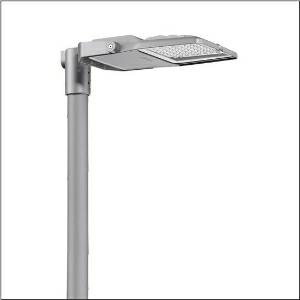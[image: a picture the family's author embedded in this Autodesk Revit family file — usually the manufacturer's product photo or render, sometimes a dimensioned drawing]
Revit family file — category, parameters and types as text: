
# Revit family: floodlight_fl_21_mini___pl64_5xa7776b4e3a_6864
name_source: partatom
category: Lighting Fixtures
units: mm (PartAtom-declared; Revit-internal decimal feet)

## family parameters
Cut with Voids When Loaded = No
Host = Face
Light Source = No
Part Type = Normal
Room Calculation Point = No
Round Connector Dimension = Use Diameter
Shared = No

## types (1)
- --- (1 x LED, 6260 lm, 45.7 W, 4000K)
    Apparent Load = 46 VA
    CIE Flux Codes = 28 80 98 100 100
    Color Rendering = 70
    Color Temperature = 4000K
    Default Elevation = 1800 mm
    Description = Floodlight FL 21 mini, floodlight, primary light control with lens, of PMMA, primary optical cover: protective disc, of toughened safety glass, transparent, light distribution: PL64, light emission: direct distribution, installation type: surface-mounted, LED, High Power LED, rated luminous flux: 6.260lm, luminous efficacy: 137lm/W, light colour: 740, colour temperature: 4000K, control gear: D4iSmart Interface (Zhaga), control: overheat protection, constant luminous flux control, time-dependent luminous flux control, flexible luminous flux parameterisation, pre-setting: logarithmic dimming characteristic, with terminal, 6-pole, mains connection: 220..240V, AC, 50/60Hz, start of lifetime: 46W, end of service life: 48W, reduction: 22W, mast bracket, of diecast aluminium, powder-coated, Siteco® metallic grey (DB 702S), corrosivity category C5 mid according to DIN EN ISO 12944, suitable for swimming pools, chlorine-resistant, sealing non-destructively replaceable, mast bracket, of steel, galvanised, powder-coated, Siteco® metallic grey (DB 702S), Smart Interface below and above, protection rating (complete): IP66, insulation class (complete): insulation class II (safety insulation), certification: CE, ENEC, VDE, protection symbol: D, impact resistance: IK08, permissible operating ambient temperature: -40..+40°C, permissible operating ambient temperature for outdoor applications: -40..+50°C, standard: DIN EN 12944, LABS conformity tested according to VDMA 24364:2018-05, packaging unit: 1 piece

Light Distribution: PL64
    Height = 70 mm
    Lamp = 1 x LED
    Lamp Light Flux = 6260 lm
    Lamp Power = 45.7 W
    Lamp count = 1
    Length = 485 mm
    Luminous efficacy = 137 lm/W
    Manufacturer = Siteco
    ModVariant = No
    Model = 5XA7776B4E3A
    Number of Poles = 1
    OnlyDefault = Yes
    Power Factor = 1
    Product Name = Floodlight FL 21 mini | PL64
    Product group = floodlight | pylon annexe
    ProductGroupID = 6201
    Protection Class = Protection class II
    Protection Degree = IP 66
    RLX_Detail_Level = 1
    RLX_Emergency_Light_Flux = 0 lm
    RLX_Emergency_Type = 0
    RLX_Emergency_Type_DB = No
    RlxData = <blob elided: 101081 chars, md5=6905e9d9>
    Socket = socket
    Standby Power = 0 W
    System Light Flux = 6260 lm
    System Power = 46 W
    Type Comments = factory setting: luminous flux: 100 % | dim-lin: 254 | 463 mA
    Type Image = l_1007125.jpg
    URL = http://relux.com
    VarID = @adj_118677
    Voltage = 0 V
    Weight = 0.00 kg
    Width = 337 mm

## geometry (parser evidence)
native form markers: Blend x4, Sweep x13
no freeform markers — native parametric forms only
